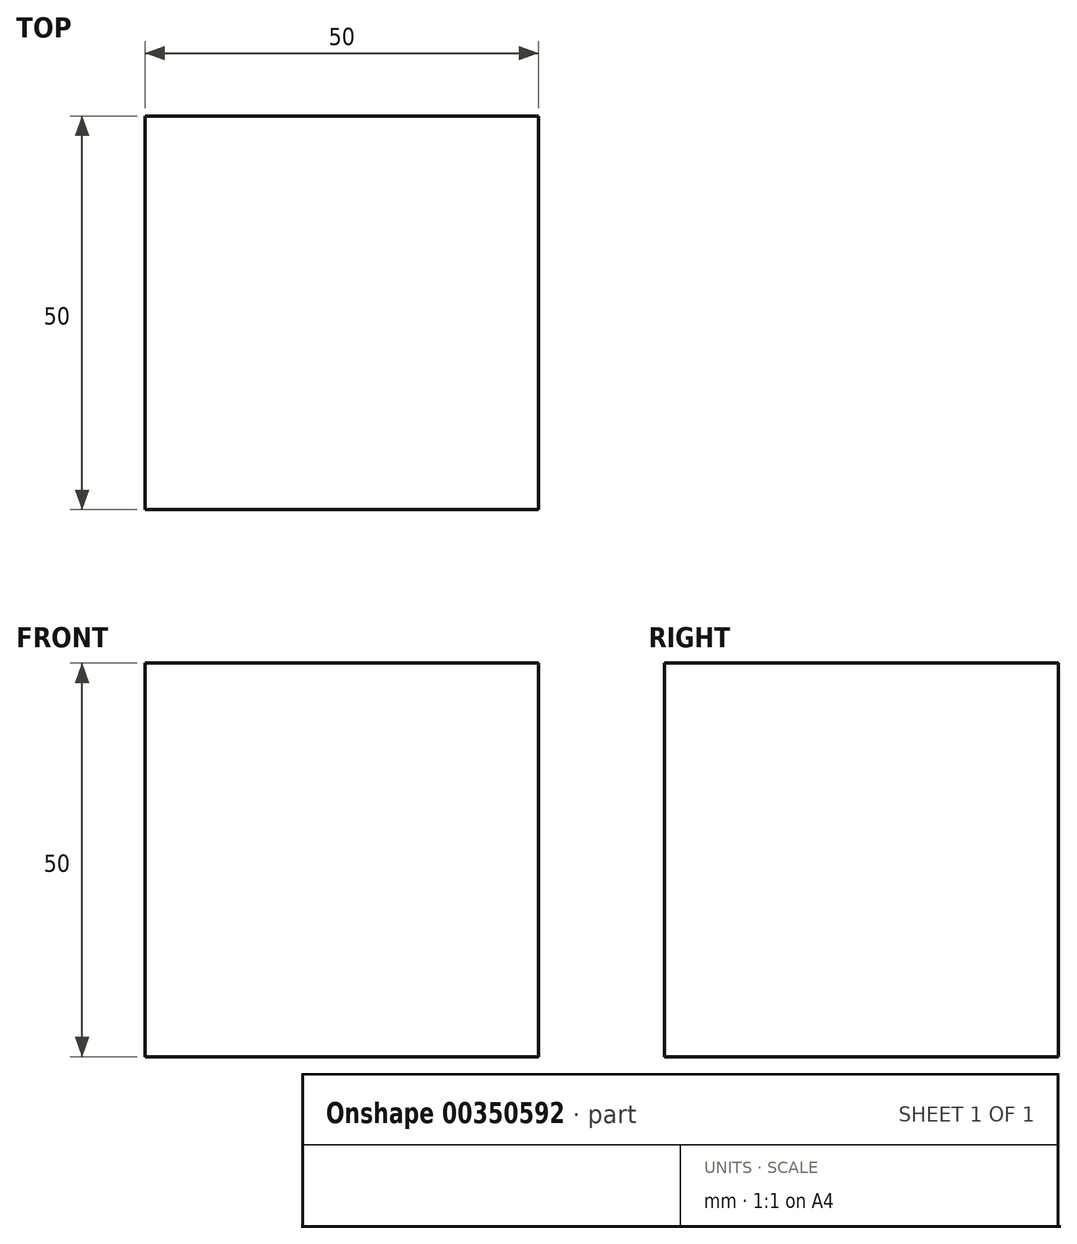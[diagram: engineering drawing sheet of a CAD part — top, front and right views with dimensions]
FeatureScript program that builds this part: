
annotation { "Feature Type Name" : "Feature", "Feature Type Description" : "" }
export const myFeature = defineFeature(function(context is Context, id is Id, definition is map)
    precondition{}
    {
        {
            var Q0;
            Q0=qCreatedBy(makeId("Top.planeOp"),FACE);
            var sketch = newSketch(context, id + "F0", { "sketchPlane" : qUnion([Q0])});
            skLineSegment(sketch, "E0.bottom", {"start": v(-30.35, 32.36) * mm, "end": v(19.65, 32.36) * mm});
            skLineSegment(sketch, "E0.top", {"start": v(-30.35, -17.64) * mm, "end": v(19.65, -17.64) * mm});
            skLineSegment(sketch, "E0.left", {"start": v(-30.35, 32.36) * mm, "end": v(-30.35, -17.64) * mm});
            skLineSegment(sketch, "E0.right", {"start": v(19.65, 32.36) * mm, "end": v(19.65, -17.64) * mm});
            skSolve(sketch);
        }
        {
            var Q0;
            Q0=makeQuery(id+"F0.imprint","IMPRINT",FACE,{"disambiguationData":[TD([[makeQuery(id+"F0.imprint","IMPRINT",EDGE,{"derivedFrom":sQuery(id+"F0.wireOp",EDGE,"E0.bottom")}),-1.0]])]});
            extrude(context, id + "F1", {"entities" : qUnion([Q0]), "depth" : 50 * mm});
        }
    });
